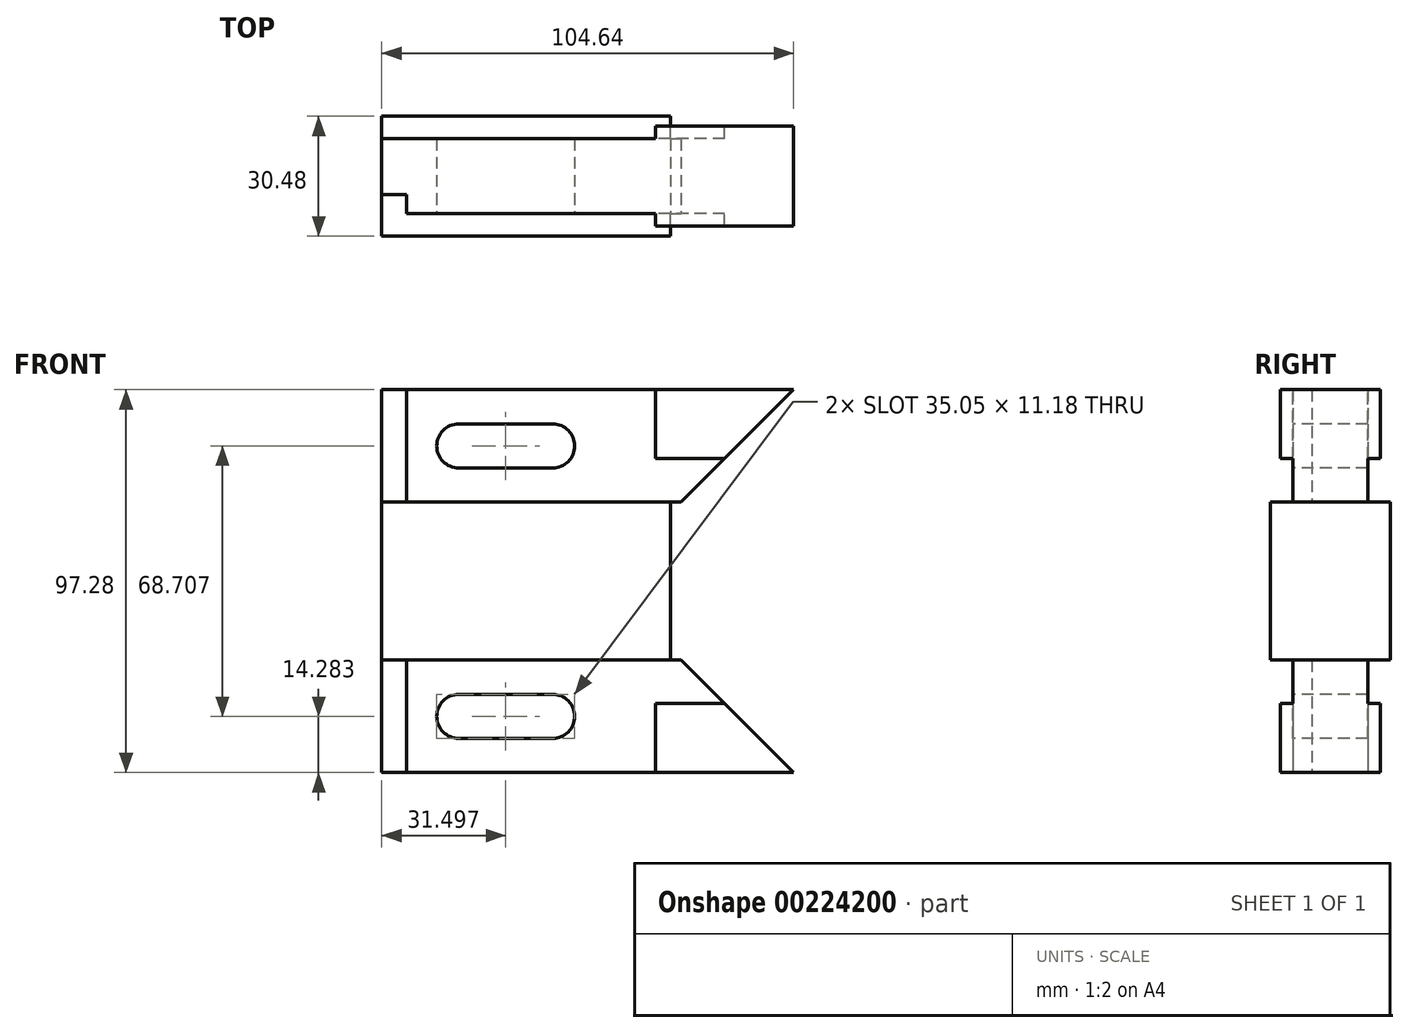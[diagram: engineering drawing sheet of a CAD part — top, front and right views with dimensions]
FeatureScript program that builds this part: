
annotation { "Feature Type Name" : "Feature", "Feature Type Description" : "" }
export const myFeature = defineFeature(function(context is Context, id is Id, definition is map)
    precondition{}
    {
        {
            var Q0;
            Q0=qCreatedBy(makeId("Front.planeOp"),FACE);
            var sketch = newSketch(context, id + "F0", { "sketchPlane" : qUnion([Q0])});
            skLineSegment(sketch, "E0.bottom", {"start": v(-52.32, 14.29) * mm, "end": v(52.32, 14.29) * mm});
            skLineSegment(sketch, "E0.top", {"start": v(-52.32, -14.29) * mm, "end": v(23.75, -14.29) * mm});
            skLineSegment(sketch, "E0.left", {"start": v(-52.32, 14.29) * mm, "end": v(-52.32, -14.29) * mm});
            skPoint(sketch, "E0.middle", {"position": v(0, 0) * mm});
            skLineSegment(sketch, "E1.bottom", {"start": v(-52.32, -14.29) * mm, "end": v(21.08, -14.29) * mm});
            skLineSegment(sketch, "E1.top", {"start": v(-52.32, -34.35) * mm, "end": v(21.08, -34.35) * mm});
            skLineSegment(sketch, "E1.left", {"start": v(-52.32, -14.29) * mm, "end": v(-52.32, -34.35) * mm});
            skLineSegment(sketch, "E1.right", {"start": v(21.08, -14.29) * mm, "end": v(21.08, -34.35) * mm});
            skLineSegment(sketch, "E2", {"start": v(-45.97, 14.29) * mm, "end": v(-45.97, -14.29) * mm});
            skLineSegment(sketch, "E3", {"start": v(52.32, 14.29) * mm, "end": v(23.75, -14.29) * mm});
            skLineSegment(sketch, "E4", {"start": v(17.27, 14.29) * mm, "end": v(17.27, -3.24) * mm});
            skLineSegment(sketch, "E5", {"start": v(17.27, -3.24) * mm, "end": v(34.8, -3.24) * mm});
            skLineSegment(sketch, "E6.bottom", {"start": v(-8.88, 5.59) * mm, "end": v(-32.76, 5.59) * mm});
            skLineSegment(sketch, "E6.top", {"start": v(-8.88, -5.59) * mm, "end": v(-32.76, -5.59) * mm});
            skPoint(sketch, "E6.middle", {"position": v(-20.82, 0) * mm});
            skArc(sketch, "E7", {"start": v(-32.76, 5.59) * mm, "mid": v(-38.35, 0) * mm, "end": v(-32.76, -5.59) * mm});
            skArc(sketch, "E8", {"start": v(-8.88, -5.59) * mm, "mid": v(-3.3, 0) * mm, "end": v(-8.88, 5.59) * mm});
            skLineSegment(sketch, "E9", {"start": v(23.75, -14.29) * mm, "end": v(52.32, -14.29) * mm});
            skLineSegment(sketch, "E10", {"start": v(52.32, -14.29) * mm, "end": v(52.32, 14.29) * mm});
            skLineSegment(sketch, "E11.MirrorCS", {"start": v(-52.32, -54.42) * mm, "end": v(21.08, -54.42) * mm});
            skLineSegment(sketch, "E12.MirrorCS", {"start": v(-52.32, -54.42) * mm, "end": v(-52.32, -34.35) * mm});
            skLineSegment(sketch, "E13.MirrorCS", {"start": v(21.08, -54.42) * mm, "end": v(21.08, -34.35) * mm});
            skLineSegment(sketch, "E14.MirrorCS", {"start": v(23.75, -54.42) * mm, "end": v(52.32, -54.42) * mm});
            skLineSegment(sketch, "E15.MirrorCS", {"start": v(52.32, -54.42) * mm, "end": v(52.32, -83) * mm});
            skLineSegment(sketch, "E16.MirrorCS", {"start": v(-52.32, -83) * mm, "end": v(52.32, -83) * mm});
            skLineSegment(sketch, "E17.MirrorCS", {"start": v(-52.32, -83) * mm, "end": v(-52.32, -54.42) * mm});
            skLineSegment(sketch, "E18.MirrorCS", {"start": v(-45.97, -83) * mm, "end": v(-45.97, -54.42) * mm});
            skLineSegment(sketch, "E19.MirrorCS", {"start": v(17.27, -83) * mm, "end": v(17.27, -65.47) * mm});
            skLineSegment(sketch, "E20.MirrorCS", {"start": v(17.27, -65.47) * mm, "end": v(34.8, -65.47) * mm});
            skLineSegment(sketch, "E21.MirrorCS", {"start": v(-8.88, -74.3) * mm, "end": v(-32.76, -74.3) * mm});
            skLineSegment(sketch, "E22.MirrorCS", {"start": v(-8.88, -63.12) * mm, "end": v(-32.76, -63.12) * mm});
            skArc(sketch, "E23.MirrorCS", {"start": v(-8.88, -63.12) * mm, "mid": v(-3.3, -68.7) * mm, "end": v(-8.88, -74.3) * mm});
            skArc(sketch, "E24.MirrorCS", {"start": v(-32.76, -74.3) * mm, "mid": v(-38.35, -68.7) * mm, "end": v(-32.76, -63.12) * mm});
            skPoint(sketch, "E25.MirrorP", {"position": v(-20.82, -68.7) * mm});
            skLineSegment(sketch, "E26.MirrorCS", {"start": v(-52.32, -54.42) * mm, "end": v(23.75, -54.42) * mm});
            skLineSegment(sketch, "E27.MirrorCS", {"start": v(52.32, -83) * mm, "end": v(23.75, -54.42) * mm});
            skPoint(sketch, "E28.MirrorP", {"position": v(0, -68.7) * mm});
            skSolve(sketch);
        }
        {
            var Q0;
            Q0 = qSketchRegion(id + "F0", true);
            extrude(context, id + "F1", {"entities" : qUnion([Q0]), "endBound" : BoundingType.SYMMETRIC, "oppositeDirection" : true, "depth" : 19.05 * mm});
        }
        {
            var Q0;
            {var subQ3=sQuery(id+"F0.wireOp",EDGE,"E9");Q0=makeQuery(id+"F0.imprint","IMPRINT",FACE,{"disambiguationData":[TD([[makeQuery(id+"F0.imprint","IMPRINT",EDGE,{"derivedFrom":subQ3}),1.0]])]});}
            extrude(context, id + "F2", {"entities" : qUnion([Q0]), "operationType" : NewBodyOperationType.REMOVE, "endBound" : BoundingType.SYMMETRIC, "oppositeDirection" : true, "depth" : 25.4 * mm});
        }
        {
            var Q0;
            Q0=makeQuery(id+"F0.imprint","IMPRINT",FACE,{"disambiguationData":[TD([[makeQuery(id+"F0.imprint","IMPRINT",EDGE,{"derivedFrom":sQuery(id+"F0.wireOp",EDGE,"E1.top")}),1.0]])]});
            extrude(context, id + "F3", {"entities" : qUnion([Q0]), "operationType" : NewBodyOperationType.ADD, "endBound" : BoundingType.SYMMETRIC, "depth" : 30.48 * mm});
        }
        {
            var Q0;
            {var subQ3=sQuery(id+"F0.wireOp",EDGE,"E4");Q0=makeQuery(id+"F0.imprint","IMPRINT",FACE,{"disambiguationData":[TD([[makeQuery(id+"F0.imprint","IMPRINT",EDGE,{"derivedFrom":subQ3}),1.0]])]});}
            extrude(context, id + "F4", {"entities" : qUnion([Q0]), "operationType" : NewBodyOperationType.ADD, "endBound" : BoundingType.SYMMETRIC, "depth" : 25.4 * mm});
        }
        {
            var Q0;
            Q0=makeQuery(id+"F1.opExtrude","CAP_FACE",FACE,{"disambiguationData":[OSD([sQuery(id+"F0.wireOp",EDGE,"E0.bottom"),sQuery(id+"F0.wireOp",EDGE,"E0.top"),sQuery(id+"F0.wireOp",EDGE,"E0.left"),sQuery(id+"F0.wireOp",EDGE,"E1.top"),sQuery(id+"F0.wireOp",EDGE,"E1.left"),sQuery(id+"F0.wireOp",EDGE,"E1.right"),sQuery(id+"F0.wireOp",EDGE,"E6.bottom"),sQuery(id+"F0.wireOp",EDGE,"E6.top"),sQuery(id+"F0.wireOp",EDGE,"E7"),sQuery(id+"F0.wireOp",EDGE,"E8"),sQuery(id+"F0.wireOp",EDGE,"E9"),sQuery(id+"F0.wireOp",EDGE,"E10")])],"isStart":true});
            var sketch = newSketch(context, id + "F5", { "sketchPlane" : qUnion([Q0])});
            skLineSegment(sketch, "E29.bottom", {"start": v(-52.32, 14.29) * mm, "end": v(-45.97, 14.29) * mm});
            skLineSegment(sketch, "E29.top", {"start": v(-52.32, -14.29) * mm, "end": v(-45.97, -14.29) * mm});
            skLineSegment(sketch, "E29.left", {"start": v(-52.32, 14.29) * mm, "end": v(-52.32, -14.29) * mm});
            skLineSegment(sketch, "E29.right", {"start": v(-45.97, 14.29) * mm, "end": v(-45.97, -14.29) * mm});
            skSolve(sketch);
        }
        {
            var Q0;
            Q0 = qSketchRegion(id + "F5", true);
            extrude(context, id + "F6", {"entities" : qUnion([Q0]), "operationType" : NewBodyOperationType.REMOVE, "oppositeDirection" : true, "depth" : 4.83 * mm});
        }
        {
            var Q0;
            {var subQ0=sQuery(id+"F0.wireOp",EDGE,"E15.MirrorCS");Q0=makeQuery(id+"F0.imprint","IMPRINT",FACE,{"disambiguationData":[TD([[makeQuery(id+"F0.imprint","IMPRINT",EDGE,{"derivedFrom":subQ0}),-1.0]])]});}
            extrude(context, id + "F7", {"entities" : qUnion([Q0]), "operationType" : NewBodyOperationType.REMOVE, "endBound" : BoundingType.SYMMETRIC, "oppositeDirection" : true, "depth" : 25.4 * mm});
        }
        {
            var Q0;
            Q0=makeQuery(id+"F0.imprint","IMPRINT",FACE,{"disambiguationData":[TD([[makeQuery(id+"F0.imprint","IMPRINT",EDGE,{"derivedFrom":sQuery(id+"F0.wireOp",EDGE,"E1.top")}),-1.0]])]});
            extrude(context, id + "F8", {"entities" : qUnion([Q0]), "operationType" : NewBodyOperationType.ADD, "endBound" : BoundingType.SYMMETRIC, "depth" : 30.48 * mm});
        }
        {
            var Q0;
            {var subQ4=sQuery(id+"F0.wireOp",EDGE,"E20.MirrorCS");Q0=makeQuery(id+"F0.imprint","IMPRINT",FACE,{"disambiguationData":[TD([[makeQuery(id+"F0.imprint","IMPRINT",EDGE,{"derivedFrom":subQ4}),-1.0]])]});}
            extrude(context, id + "F9", {"entities" : qUnion([Q0]), "operationType" : NewBodyOperationType.ADD, "endBound" : BoundingType.SYMMETRIC, "depth" : 25.4 * mm});
        }
        {
            var Q0;
            {var subQ0=sQuery(id+"F0.wireOp",EDGE,"E24.MirrorCS");var subQ1=sQuery(id+"F0.wireOp",EDGE,"E23.MirrorCS");var subQ2=sQuery(id+"F0.wireOp",EDGE,"E15.MirrorCS");var subQ3=sQuery(id+"F0.wireOp",EDGE,"E21.MirrorCS");var subQ4=sQuery(id+"F0.wireOp",EDGE,"E22.MirrorCS");var subQ5=sQuery(id+"F0.wireOp",EDGE,"E17.MirrorCS");var subQ6=sQuery(id+"F0.wireOp",EDGE,"E12.MirrorCS");var subQ7=sQuery(id+"F0.wireOp",EDGE,"E1.left");var subQ8=sQuery(id+"F0.wireOp",EDGE,"E0.left");var subQ9=sQuery(id+"F0.wireOp",EDGE,"E14.MirrorCS");var subQ10=sQuery(id+"F0.wireOp",EDGE,"E26.MirrorCS");var subQ11=sQuery(id+"F0.wireOp",EDGE,"E13.MirrorCS");var subQ12=sQuery(id+"F0.wireOp",EDGE,"E1.right");var subQ13=sQuery(id+"F0.wireOp",EDGE,"E16.MirrorCS");Q0=makeQuery(id+"F3.boolean.opBoolean","SPLIT",FACE,{"disambiguationData":[TD([makeQuery(id+"F1.opExtrude","SWEPT_FACE",FACE,{"disambiguationData":[OSD([subQ13])]})])],"derivedFrom":makeQuery(id+"F1.opExtrude","CAP_FACE",FACE,{"disambiguationData":[OSD([sQuery(id+"F0.wireOp",EDGE,"E0.bottom"),sQuery(id+"F0.wireOp",EDGE,"E0.top"),subQ8,subQ7,subQ12,sQuery(id+"F0.wireOp",EDGE,"E6.bottom"),sQuery(id+"F0.wireOp",EDGE,"E6.top"),sQuery(id+"F0.wireOp",EDGE,"E7"),sQuery(id+"F0.wireOp",EDGE,"E8"),sQuery(id+"F0.wireOp",EDGE,"E9"),sQuery(id+"F0.wireOp",EDGE,"E10"),subQ6,subQ11,subQ10,subQ13,subQ3,subQ2,subQ1,subQ4,subQ5,subQ9,subQ0])],"isStart":true})});}
            var sketch = newSketch(context, id + "F10", { "sketchPlane" : qUnion([Q0])});
            skLineSegment(sketch, "E30.bottom", {"start": v(-52.32, -54.42) * mm, "end": v(-45.97, -54.42) * mm});
            skLineSegment(sketch, "E30.top", {"start": v(-52.32, -83) * mm, "end": v(-45.97, -83) * mm});
            skLineSegment(sketch, "E30.left", {"start": v(-52.32, -54.42) * mm, "end": v(-52.32, -83) * mm});
            skLineSegment(sketch, "E30.right", {"start": v(-45.97, -54.42) * mm, "end": v(-45.97, -83) * mm});
            skSolve(sketch);
        }
        {
            var Q0;
            Q0=makeQuery(id+"F10.imprint","IMPRINT",FACE,{"disambiguationData":[TD([[makeQuery(id+"F10.imprint","IMPRINT",EDGE,{"derivedFrom":sQuery(id+"F10.wireOp",EDGE,"E30.bottom")}),1.0]])]});
            extrude(context, id + "F11", {"entities" : qUnion([Q0]), "operationType" : NewBodyOperationType.REMOVE, "oppositeDirection" : true, "depth" : 4.83 * mm});
        }
    });
